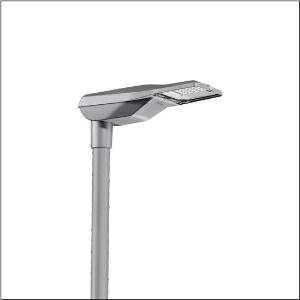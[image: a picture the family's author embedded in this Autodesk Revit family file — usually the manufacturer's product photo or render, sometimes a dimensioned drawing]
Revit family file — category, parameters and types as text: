
# Revit family: streetlight_sl_21_iq_micro___st1_0a_5xe1d31g08db_9cf9
name_source: partatom
category: Lighting Fixtures
units: mm (PartAtom-declared; Revit-internal decimal feet)

## family parameters
Cut with Voids When Loaded = No
Host = Face
Light Source = No
Part Type = Normal
Room Calculation Point = No
Round Connector Dimension = Use Diameter
Shared = No

## types (1)
- --- (1 x LED, 4810 lm, 36.4 W, 3000K)
    Apparent Load = 36 VA
    CIE Flux Codes = 37 72 97 100 100
    Color Rendering = 70
    Color Temperature = 3000K
    Default Elevation = 1800 mm
    Description = Streetlight SL 21 iQ micro, mast luminaire, primary light control with lens, of PMMA, primary optical cover: cover, of toughened safety glass, transparent, light distribution: ST1.0a, light emission: direct distribution, primary light characteristic: asymmetric, installation type: post-top, side-entry, LED, High Power LED, rated luminous flux: 4.810lm, luminous efficacy: 132lm/W, light colour: 730, colour temperature: 3000K, control: Street-Remote, Auto-Match, Temp-Guard, Lumen-Switch, Night-Set, Smart-Wire, Light-Fading, Desk-Remote (wireless, voltage-free reading and setting of iQ features in the workshop via application-optimized NFC function/RFID function), optimised constant luminous flux control (CLO 2.0), presetting dimming linear, mains connection: 220..240V, AC, 50/60Hz, start of lifetime: 36W, end of service life: 38W, reduction: 16W, luminaire housing, of diecast aluminium, powder-coated, Siteco® metallic grey (DB 702S), corrosivity category C5 mid according to DIN EN ISO 12944, please order mast flange separately, inclination adjustable: 0°, 5°, 10°, 15°, sealing non-destructively replaceable, multi-level sealing system, length: 528mm, width: 235mm, height: 110mm, mast flange for spigot size: 42mm (side-entry): 5XC10008XM4, 60/48mm (side-entry/post-top): 5XC10108XM2, 76/60mm (side-entry/post-top): 5XC10108XM1, protection rating (complete): IP66, insulation class (complete): insulation class II (safety insulation), certification: CE, ENEC, ENEC+, VDE, impact resistance: IK09, permissible operating ambient temperature for outdoor applications: -40..+50°C, standard-compliant lighting for roads and squares, packaging unit: 1 piece

Light Distribution: ST1.0a
    Height = 110 mm
    Lamp = 1 x LED
    Lamp Light Flux = 4810 lm
    Lamp Power = 36.4 W
    Lamp count = 1
    Length = 528 mm
    Luminous efficacy = 132 lm/W
    Manufacturer = Siteco
    ModVariant = No
    Model = 5XE1D31G08DB
    Number of Poles = 1
    OnlyDefault = Yes
    Power Factor = 1
    Product Name = Streetlight SL 21 iQ micro | ST1.0a
    Product group = mast luminaire | pylon top
    ProductGroupID = 6100
    Protection Class = Protection class II
    Protection Degree = IP 66
    RLX_Detail_Level = 1
    RLX_Emergency_Light_Flux = 0 lm
    RLX_Emergency_Type = 0
    RLX_Emergency_Type_DB = No
    RlxData = <blob elided: 98753 chars, md5=c3ccf49a>
    Socket = socket
    Standby Power = 0 W
    System Light Flux = 4810 lm
    System Power = 36 W
    Type Comments = factory setting: luminous flux: 100 % | dim-lin: 254 | 715 mA
    Type Image = l_1006881.jpg
    URL = http://relux.com
    VarID = @adj_106143
    Voltage = 0 V
    Weight = 0.00 kg
    Width = 235 mm

## geometry (parser evidence)
native form markers: Blend x4, Sweep x10
no freeform markers — native parametric forms only
